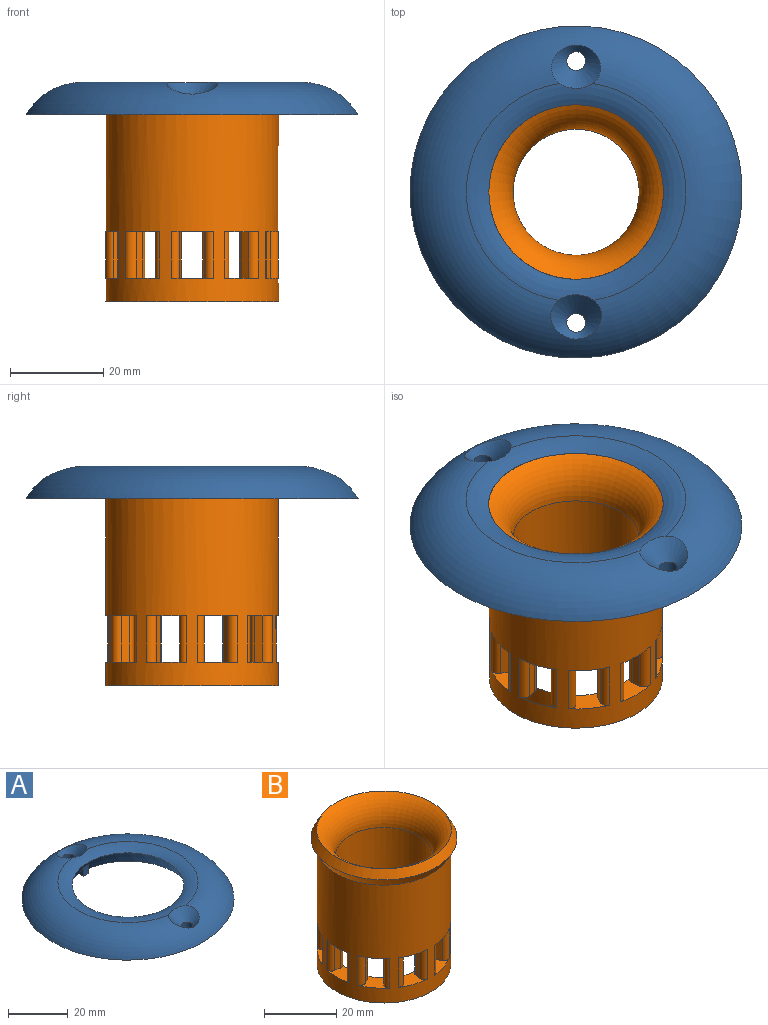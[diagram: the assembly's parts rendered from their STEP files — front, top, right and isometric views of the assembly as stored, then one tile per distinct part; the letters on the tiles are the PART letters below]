
ASSEMBLY  parts=2 mates=1
PART A: 11 faces, bbox 81.2x81.2x14.1 mm
  f0: torus R=23.5mm, axis (0,0,1), area 2602.4mm2, adj f1,f3,f8,f9
  f1: torus R=23.5mm, axis (0,0,1), area 650.6mm2, adj f0,f2,f8,f9
  f2: cone r=18.5mm half-angle=30deg, axis (0,0,-1), area 828mm2, adj f1,f3,f4,f5,f6
  f3: plane 71.08x71.08mm, normal (0,0,-1), area 2433.3mm2, adj f0,f2,f4,f5,f6,f7,f10
  f4: plane 4x2.67mm, normal (0,-1,0), area 9.5mm2, adj f2,f3,f5,f6
  f5: plane 3.77x2.19mm, normal (1,0,0), area 4.1mm2, adj f2,f3,f4
  f6: plane 3.77x2.19mm, normal (-1,0,0), area 4.1mm2, adj f2,f3,f4
  f7: cylinder r=2mm len=4mm, axis (0,0,1), area 37.7mm2, adj f3,f8
  f8: cone r=2mm half-angle=45deg, axis (0,0,1), area 91mm2, adj f0,f1,f7
  f9: cone r=2mm half-angle=46.3deg, axis (0,0,1), area 94.6mm2, adj f0,f1,f10
  f10: cylinder r=2mm len=4mm, axis (0,0,1), area 37.7mm2, adj f3,f9
PART B: 89 faces, bbox 50.9x50.9x47 mm
  f0: cone r=18.5mm half-angle=30deg, axis (0,0,1), area 413.8mm2, adj f1,f4,f86,f87,f88
  f1: cone r=18.5mm half-angle=30deg, axis (0,0,-1), area 371.9mm2, adj f0,f2,f86,f87,f88
  f2: torus R=23.5mm, axis (0,0,1), area 1026.1mm2, adj f1,f3
  f3: cylinder r=13.5mm len=36.93mm, axis (0,0,1), area 2437.8mm2, adj f2,f5,f8,f9,f12,f13,f15,f16
  f4: cylinder r=18.5mm len=40mm, axis (0,0,1), area 3741.5mm2, adj f0,f5,f8,f9,f12,f13,f15,f16
  f5: plane 37x37mm, normal (0,0,-1), area 502.7mm2, adj f3,f4
  f6: plane 10x1.79mm, normal (0.45,-0.89,0), area 20.1mm2, adj f8,f9,f23,f25
  f7: plane 10x1.42mm, normal (-0.71,0.71,0), area 20.1mm2, adj f8,f9,f24,f26
  f8: plane 9.29x8.62mm, normal (0,0,1), area 27.1mm2, adj f3,f4,f6,f7,f23,f24,f25,f26
  f9: plane 9.29x8.62mm, normal (0,0,-1), area 27.1mm2, adj f3,f4,f6,f7,f23,f24,f25,f26
  f10: plane 10x1.79mm, normal (0.89,-0.45,0), area 20.1mm2, adj f12,f13,f19,f21
  f11: plane 10x1.98mm, normal (-0.99,0.16,0), area 20.1mm2, adj f12,f13,f20,f22
  f12: plane 9.05x7.1mm, normal (0,0,1), area 27.1mm2, adj f3,f4,f10,f11,f19,f20,f21,f22
  f13: plane 9.05x7.1mm, normal (0,0,-1), area 27.1mm2, adj f3,f4,f10,f11,f19,f20,f21,f22
  f14: plane 10x1.98mm, normal (-0.16,0.99,0), area 20.1mm2, adj f15,f16,f17,f18
  f15: plane 8.99x5.44mm, normal (0,0,1), area 27.1mm2, adj f3,f4,f14,f17,f18,f35,f36,f37
  f16: plane 8.99x5.44mm, normal (0,0,-1), area 27.1mm2, adj f3,f4,f14,f17,f18,f35,f36,f37
  f17: cylinder r=1.5mm len=10mm, axis (0,0,1), area 24.9mm2, adj f4,f14,f15,f16
  f18: cylinder r=1.5mm len=10mm, axis (0,0,1), area 22.1mm2, adj f3,f14,f15,f16
  f19: cylinder r=1.5mm len=10mm, axis (0,0,1), area 24.9mm2, adj f4,f10,f12,f13
  f20: cylinder r=1.5mm len=10mm, axis (0,0,1), area 24.9mm2, adj f4,f11,f12,f13
  f21: cylinder r=1.5mm len=10mm, axis (0,0,1), area 22.1mm2, adj f3,f10,f12,f13
  f22: cylinder r=1.5mm len=10mm, axis (0,0,1), area 22.1mm2, adj f3,f11,f12,f13
  f23: cylinder r=1.5mm len=10mm, axis (0,0,1), area 24.9mm2, adj f4,f6,f8,f9
  f24: cylinder r=1.5mm len=10mm, axis (0,0,1), area 24.9mm2, adj f4,f7,f8,f9
  f25: cylinder r=1.5mm len=10mm, axis (0,0,1), area 22.1mm2, adj f3,f6,f8,f9
  f26: cylinder r=1.5mm len=10mm, axis (0,0,1), area 22.1mm2, adj f3,f7,f8,f9
  f27: plane 10x1.79mm, normal (0.45,0.89,0), area 20.1mm2, adj f29,f30,f42,f44
  f28: plane 10x1.42mm, normal (-0.71,-0.71,0), area 20.1mm2, adj f29,f30,f43,f45
  f29: plane 9.29x8.62mm, normal (0,0,1), area 27.1mm2, adj f3,f4,f27,f28,f42,f43,f44,f45
  f30: plane 9.29x8.62mm, normal (0,0,-1), area 27.1mm2, adj f3,f4,f27,f28,f42,f43,f44,f45
  f31: plane 10x1.79mm, normal (0.89,0.45,0), area 20.1mm2, adj f33,f34,f38,f40
  f32: plane 10x1.98mm, normal (-0.99,-0.16,0), area 20.1mm2, adj f33,f34,f39,f41
  f33: plane 9.05x7.1mm, normal (0,0,1), area 27.1mm2, adj f3,f4,f31,f32,f38,f39,f40,f41
  f34: plane 9.05x7.1mm, normal (0,0,-1), area 27.1mm2, adj f3,f4,f31,f32,f38,f39,f40,f41
  f35: plane 10x1.98mm, normal (-0.16,-0.99,0), area 20.1mm2, adj f15,f16,f36,f37
  f36: cylinder r=1.5mm len=10mm, axis (0,0,1), area 24.9mm2, adj f4,f15,f16,f35
  f37: cylinder r=1.5mm len=10mm, axis (0,0,1), area 22.1mm2, adj f3,f15,f16,f35
  f38: cylinder r=1.5mm len=10mm, axis (0,0,1), area 24.9mm2, adj f4,f31,f33,f34
  f39: cylinder r=1.5mm len=10mm, axis (0,0,1), area 24.9mm2, adj f4,f32,f33,f34
  f40: cylinder r=1.5mm len=10mm, axis (0,0,1), area 22.1mm2, adj f3,f31,f33,f34
  f41: cylinder r=1.5mm len=10mm, axis (0,0,1), area 22.1mm2, adj f3,f32,f33,f34
  f42: cylinder r=1.5mm len=10mm, axis (0,0,1), area 24.9mm2, adj f4,f27,f29,f30
  f43: cylinder r=1.5mm len=10mm, axis (0,0,1), area 24.9mm2, adj f4,f28,f29,f30
  f44: cylinder r=1.5mm len=10mm, axis (0,0,1), area 22.1mm2, adj f3,f27,f29,f30
  f45: cylinder r=1.5mm len=10mm, axis (0,0,1), area 22.1mm2, adj f3,f28,f29,f30
  f46: plane 10x1.79mm, normal (-0.45,-0.89,0), area 20.1mm2, adj f48,f49,f63,f65
  f47: plane 10x1.42mm, normal (0.71,0.71,0), area 20.1mm2, adj f48,f49,f64,f66
  f48: plane 9.29x8.62mm, normal (0,0,1), area 27.1mm2, adj f3,f4,f46,f47,f63,f64,f65,f66
  f49: plane 9.29x8.62mm, normal (0,0,-1), area 27.1mm2, adj f3,f4,f46,f47,f63,f64,f65,f66
  f50: plane 10x1.79mm, normal (-0.89,-0.45,0), area 20.1mm2, adj f52,f53,f59,f61
  f51: plane 10x1.98mm, normal (0.99,0.16,0), area 20.1mm2, adj f52,f53,f60,f62
  f52: plane 9.05x7.1mm, normal (0,0,1), area 27.1mm2, adj f3,f4,f50,f51,f59,f60,f61,f62
  f53: plane 9.05x7.1mm, normal (0,0,-1), area 27.1mm2, adj f3,f4,f50,f51,f59,f60,f61,f62
  f54: plane 10x1.98mm, normal (0.16,0.99,0), area 20.1mm2, adj f55,f56,f57,f58
  f55: plane 8.99x5.44mm, normal (0,0,1), area 27.1mm2, adj f3,f4,f54,f57,f58,f75,f76,f77
  f56: plane 8.99x5.44mm, normal (0,0,-1), area 27.1mm2, adj f3,f4,f54,f57,f58,f75,f76,f77
  f57: cylinder r=1.5mm len=10mm, axis (0,0,1), area 24.9mm2, adj f4,f54,f55,f56
  f58: cylinder r=1.5mm len=10mm, axis (0,0,1), area 22.1mm2, adj f3,f54,f55,f56
  f59: cylinder r=1.5mm len=10mm, axis (0,0,1), area 24.9mm2, adj f4,f50,f52,f53
  f60: cylinder r=1.5mm len=10mm, axis (0,0,1), area 24.9mm2, adj f4,f51,f52,f53
  f61: cylinder r=1.5mm len=10mm, axis (0,0,1), area 22.1mm2, adj f3,f50,f52,f53
  f62: cylinder r=1.5mm len=10mm, axis (0,0,1), area 22.1mm2, adj f3,f51,f52,f53
  f63: cylinder r=1.5mm len=10mm, axis (0,0,1), area 24.9mm2, adj f4,f46,f48,f49
  f64: cylinder r=1.5mm len=10mm, axis (0,0,1), area 24.9mm2, adj f4,f47,f48,f49
  f65: cylinder r=1.5mm len=10mm, axis (0,0,1), area 22.1mm2, adj f3,f46,f48,f49
  f66: cylinder r=1.5mm len=10mm, axis (0,0,1), area 22.1mm2, adj f3,f47,f48,f49
  f67: plane 10x1.79mm, normal (-0.45,0.89,0), area 20.1mm2, adj f69,f70,f82,f84
  f68: plane 10x1.42mm, normal (0.71,-0.71,0), area 20.1mm2, adj f69,f70,f83,f85
  f69: plane 9.29x8.62mm, normal (0,0,1), area 27.1mm2, adj f3,f4,f67,f68,f82,f83,f84,f85
  f70: plane 9.29x8.62mm, normal (0,0,-1), area 27.1mm2, adj f3,f4,f67,f68,f82,f83,f84,f85
  f71: plane 10x1.79mm, normal (-0.89,0.45,0), area 20.1mm2, adj f73,f74,f78,f80
  f72: plane 10x1.98mm, normal (0.99,-0.16,0), area 20.1mm2, adj f73,f74,f79,f81
  f73: plane 9.05x7.1mm, normal (0,0,1), area 27.1mm2, adj f3,f4,f71,f72,f78,f79,f80,f81
  f74: plane 9.05x7.1mm, normal (0,0,-1), area 27.1mm2, adj f3,f4,f71,f72,f78,f79,f80,f81
  f75: plane 10x1.98mm, normal (0.16,-0.99,0), area 20.1mm2, adj f55,f56,f76,f77
  f76: cylinder r=1.5mm len=10mm, axis (0,0,1), area 24.9mm2, adj f4,f55,f56,f75
  f77: cylinder r=1.5mm len=10mm, axis (0,0,1), area 22.1mm2, adj f3,f55,f56,f75
  f78: cylinder r=1.5mm len=10mm, axis (0,0,1), area 24.9mm2, adj f4,f71,f73,f74
  f79: cylinder r=1.5mm len=10mm, axis (0,0,1), area 24.9mm2, adj f4,f72,f73,f74
  f80: cylinder r=1.5mm len=10mm, axis (0,0,1), area 22.1mm2, adj f3,f71,f73,f74
  f81: cylinder r=1.5mm len=10mm, axis (0,0,1), area 22.1mm2, adj f3,f72,f73,f74
  f82: cylinder r=1.5mm len=10mm, axis (0,0,1), area 24.9mm2, adj f4,f67,f69,f70
  f83: cylinder r=1.5mm len=10mm, axis (0,0,1), area 24.9mm2, adj f4,f68,f69,f70
  f84: cylinder r=1.5mm len=10mm, axis (0,0,1), area 22.1mm2, adj f3,f67,f69,f70
  f85: cylinder r=1.5mm len=10mm, axis (0,0,1), area 22.1mm2, adj f3,f68,f69,f70
  f86: plane 4.04x1.17mm, normal (0,-1,0), area 2.4mm2, adj f0,f1,f87
  f87: plane 4.35x3.28mm, normal (1,0,0), area 13.4mm2, adj f0,f1,f86,f88
  f88: plane 4.04x1.17mm, normal (0,1,0), area 2.4mm2, adj f0,f1,f87
PLACE A t=(-5.67,-5.47,-2.72)mm
PLACE B rot(axis=(0,0,1),90deg) t=(-5.67,-5.47,-2.72)mm
MATE revolute A.f0 <-> B.f0  axis (0,0,-1) through (-5.67,-5.47,-2.72)mm
